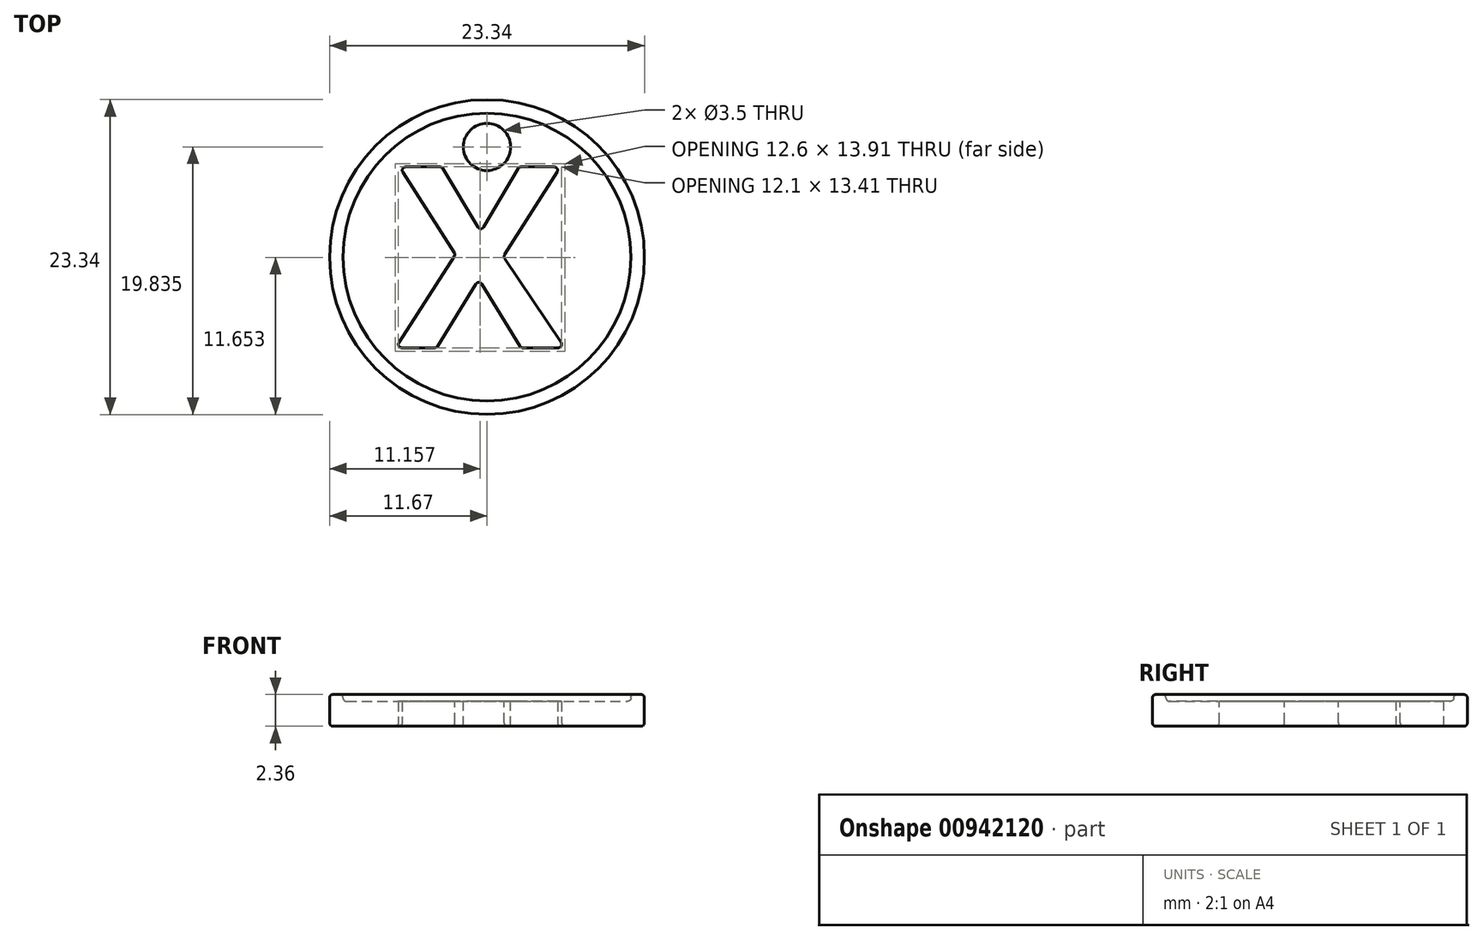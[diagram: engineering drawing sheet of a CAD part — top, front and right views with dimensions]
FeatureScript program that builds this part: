
annotation { "Feature Type Name" : "Feature", "Feature Type Description" : "" }
export const myFeature = defineFeature(function(context is Context, id is Id, definition is map)
    precondition{}
    {
        {
            var Q0;
            Q0=qCreatedBy(makeId("Front.planeOp"),FACE);
            var sketch = newSketch(context, id + "F0", { "sketchPlane" : qUnion([Q0])});
            skLineSegment(sketch, "E0", {"start": v(0, -1.17) * mm, "end": v(11.66, -1.17) * mm});
            skLineSegment(sketch, "E1", {"start": v(11.66, -1.17) * mm, "end": v(11.66, 1.17) * mm});
            skLineSegment(sketch, "E2", {"start": v(11.66, 1.17) * mm, "end": v(10.67, 1.17) * mm});
            skLineSegment(sketch, "E3", {"start": v(10.67, 1.17) * mm, "end": v(10.67, 0.67) * mm});
            skLineSegment(sketch, "E4", {"start": v(10.67, 0.67) * mm, "end": v(0, 0.67) * mm});
            skLineSegment(sketch, "E5", {"start": v(0, 0.67) * mm, "end": v(0, -1.17) * mm});
            skLineSegment(sketch, "E6", {"start": v(0, 5.9) * mm, "end": v(0, -4.97) * mm, "construction": true});
            skSolve(sketch);
        }
        {
            var Q0;
            Q0=makeQuery(id+"F0.imprint","IMPRINT",FACE,{"disambiguationData":[TD([[makeQuery(id+"F0.imprint","IMPRINT",EDGE,{"derivedFrom":sQuery(id+"F0.wireOp",EDGE,"E0")}),1.0]])]});
            var Q1;
            Q1=sQuery(id+"F0.wireOp",EDGE,"E6");
            revolve(context, id + "F1", {"surfaceOperationType" : NewSurfaceOperationType.NEW, "entities" : qUnion([Q0]), "axis" : qUnion([Q1]), "revolveType" : RevolveType.FULL});
        }
        {
            var Q0;
            Q0=makeQuery(id+"F1.opRevolve","SWEPT_FACE",FACE,{"disambiguationData":[OSD([sQuery(id+"F0.wireOp",EDGE,"E4")])]});
            var sketch = newSketch(context, id + "F2", { "sketchPlane" : qUnion([Q0])});
            skText(sketch, "E7", { "text": "X", "fontName": "OpenSans-Bold.ttf"});
            const initialGuessF2  = {"E7": [-0.00677, -0.00672, 1, 0, 0.01352]};
            skSetInitialGuess(sketch, initialGuessF2);
            skSolve(sketch);
        }
        {
            var Q0;
            Q0=makeQuery(id+"F2.imprint","IMPRINT",FACE,{"disambiguationData":[TD([[makeQuery(id+"F2.imprint","IMPRINT",EDGE,{"derivedFrom":sQuery(id+"F2.wireOp",EDGE,"E7.sketch_text.stroke-0")}),-1.0]])]});
            extrude(context, id + "F3", {"entities" : qUnion([Q0]), "operationType" : NewBodyOperationType.REMOVE, "oppositeDirection" : true, "depth" : 25 * mm, "offsetDistance" : 25 * mm});
        }
        {
            var Q0;
            Q0=makeQuery(id+"F1.opRevolve","SWEPT_EDGE",EDGE,{"disambiguationData":[OSD([sQuery(id+"F0.wireOp",EDGE,"E1"),sQuery(id+"F0.wireOp",EDGE,"E2")])]});
            var Q1;
            Q1=makeQuery(id+"F3.boolean.opBoolean","COPY",EDGE,{"derivedFrom":makeQuery(id+"F3.opExtrude","CAP_EDGE",EDGE,{"disambiguationData":[OSD([sQuery(id+"F2.wireOp",EDGE,"E7.sketch_text.stroke-5")])],"isStart":true})});
            var Q2;
            Q2=makeQuery(id+"F1.opRevolve","SWEPT_EDGE",EDGE,{"disambiguationData":[OSD([sQuery(id+"F0.wireOp",EDGE,"E0"),sQuery(id+"F0.wireOp",EDGE,"E1")])]});
            var Q3;
            Q3=makeQuery(id+"F1.opRevolve","SWEPT_EDGE",EDGE,{"disambiguationData":[OSD([sQuery(id+"F0.wireOp",EDGE,"E2"),sQuery(id+"F0.wireOp",EDGE,"E3")])]});
            var Q4;
            Q4=makeQuery(id+"F1.opRevolve","SWEPT_EDGE",EDGE,{"disambiguationData":[OSD([sQuery(id+"F0.wireOp",EDGE,"E3"),sQuery(id+"F0.wireOp",EDGE,"E4")])]});
            var Q5;
            Q5=makeQuery(id+"F3.boolean.opBoolean","COPY",EDGE,{"derivedFrom":makeQuery(id+"F3.opExtrude","CAP_EDGE",EDGE,{"disambiguationData":[OSD([sQuery(id+"F2.wireOp",EDGE,"E7.sketch_text.stroke-1")])],"isStart":true})});
            var Q6;
            Q6=makeQuery(id+"F3.boolean.opBoolean","INTERSECT",EDGE,{"derivedFrom":[makeQuery(id+"F1.opRevolve","SWEPT_FACE",FACE,{"disambiguationData":[OSD([sQuery(id+"F0.wireOp",EDGE,"E0")])]}),makeQuery(id+"F3.opExtrude","SWEPT_FACE",FACE,{"disambiguationData":[OSD([sQuery(id+"F2.wireOp",EDGE,"E7.sketch_text.stroke-7")])]})]});
            var Q7;
            Q7=makeQuery(id+"F3.boolean.opBoolean","COPY",EDGE,{"derivedFrom":makeQuery(id+"F3.opExtrude","CAP_EDGE",EDGE,{"disambiguationData":[OSD([sQuery(id+"F2.wireOp",EDGE,"E7.sketch_text.stroke-7")])],"isStart":true})});
            var Q8;
            Q8=makeQuery(id+"F3.boolean.opBoolean","INTERSECT",EDGE,{"derivedFrom":[makeQuery(id+"F1.opRevolve","SWEPT_FACE",FACE,{"disambiguationData":[OSD([sQuery(id+"F0.wireOp",EDGE,"E0")])]}),makeQuery(id+"F3.opExtrude","SWEPT_FACE",FACE,{"disambiguationData":[OSD([sQuery(id+"F2.wireOp",EDGE,"E7.sketch_text.stroke-11")])]})]});
            var Q9;
            Q9=makeQuery(id+"F3.boolean.opBoolean","COPY",EDGE,{"derivedFrom":makeQuery(id+"F3.opExtrude","CAP_EDGE",EDGE,{"disambiguationData":[OSD([sQuery(id+"F2.wireOp",EDGE,"E7.sketch_text.stroke-9")])],"isStart":true})});
            var Q10;
            Q10=makeQuery(id+"F3.boolean.opBoolean","COPY",EDGE,{"derivedFrom":makeQuery(id+"F3.opExtrude","CAP_EDGE",EDGE,{"disambiguationData":[OSD([sQuery(id+"F2.wireOp",EDGE,"E7.sketch_text.stroke-11")])],"isStart":true})});
            var Q11;
            Q11=makeQuery(id+"F3.boolean.opBoolean","COPY",EDGE,{"derivedFrom":makeQuery(id+"F3.opExtrude","CAP_EDGE",EDGE,{"disambiguationData":[OSD([sQuery(id+"F2.wireOp",EDGE,"E7.sketch_text.stroke-2")])],"isStart":true})});
            var Q12;
            Q12=makeQuery(id+"F3.boolean.opBoolean","COPY",EDGE,{"derivedFrom":makeQuery(id+"F3.opExtrude","CAP_EDGE",EDGE,{"disambiguationData":[OSD([sQuery(id+"F2.wireOp",EDGE,"E7.sketch_text.stroke-3")])],"isStart":true})});
            var Q13;
            Q13=makeQuery(id+"F3.boolean.opBoolean","COPY",EDGE,{"derivedFrom":makeQuery(id+"F3.opExtrude","SWEPT_EDGE",EDGE,{"disambiguationData":[OSD([sQuery(id+"F2.wireOp",EDGE,"E7.sketch_text.stroke-0"),sQuery(id+"F2.wireOp",EDGE,"E7.sketch_text.stroke-11")])]})});
            var Q14;
            Q14=makeQuery(id+"F3.boolean.opBoolean","COPY",EDGE,{"derivedFrom":makeQuery(id+"F3.opExtrude","SWEPT_EDGE",EDGE,{"disambiguationData":[OSD([sQuery(id+"F2.wireOp",EDGE,"E7.sketch_text.stroke-0"),sQuery(id+"F2.wireOp",EDGE,"E7.sketch_text.stroke-1")])]})});
            var Q15;
            Q15=makeQuery(id+"F3.boolean.opBoolean","COPY",EDGE,{"derivedFrom":makeQuery(id+"F3.opExtrude","SWEPT_EDGE",EDGE,{"disambiguationData":[OSD([sQuery(id+"F2.wireOp",EDGE,"E7.sketch_text.stroke-1"),sQuery(id+"F2.wireOp",EDGE,"E7.sketch_text.stroke-2")])]})});
            var Q16;
            Q16=makeQuery(id+"F3.boolean.opBoolean","COPY",EDGE,{"derivedFrom":makeQuery(id+"F3.opExtrude","SWEPT_EDGE",EDGE,{"disambiguationData":[OSD([sQuery(id+"F2.wireOp",EDGE,"E7.sketch_text.stroke-2"),sQuery(id+"F2.wireOp",EDGE,"E7.sketch_text.stroke-3")])]})});
            var Q17;
            Q17=makeQuery(id+"F3.boolean.opBoolean","COPY",EDGE,{"derivedFrom":makeQuery(id+"F3.opExtrude","SWEPT_EDGE",EDGE,{"disambiguationData":[OSD([sQuery(id+"F2.wireOp",EDGE,"E7.sketch_text.stroke-3"),sQuery(id+"F2.wireOp",EDGE,"E7.sketch_text.stroke-4")])]})});
            var Q18;
            Q18=makeQuery(id+"F3.boolean.opBoolean","COPY",EDGE,{"derivedFrom":makeQuery(id+"F3.opExtrude","SWEPT_EDGE",EDGE,{"disambiguationData":[OSD([sQuery(id+"F2.wireOp",EDGE,"E7.sketch_text.stroke-5"),sQuery(id+"F2.wireOp",EDGE,"E7.sketch_text.stroke-6")])]})});
            var Q19;
            Q19=makeQuery(id+"F3.boolean.opBoolean","COPY",EDGE,{"derivedFrom":makeQuery(id+"F3.opExtrude","SWEPT_EDGE",EDGE,{"disambiguationData":[OSD([sQuery(id+"F2.wireOp",EDGE,"E7.sketch_text.stroke-6"),sQuery(id+"F2.wireOp",EDGE,"E7.sketch_text.stroke-7")])]})});
            var Q20;
            Q20=makeQuery(id+"F3.boolean.opBoolean","COPY",EDGE,{"derivedFrom":makeQuery(id+"F3.opExtrude","SWEPT_EDGE",EDGE,{"disambiguationData":[OSD([sQuery(id+"F2.wireOp",EDGE,"E7.sketch_text.stroke-7"),sQuery(id+"F2.wireOp",EDGE,"E7.sketch_text.stroke-8")])]})});
            var Q21;
            Q21=makeQuery(id+"F3.boolean.opBoolean","COPY",EDGE,{"derivedFrom":makeQuery(id+"F3.opExtrude","SWEPT_EDGE",EDGE,{"disambiguationData":[OSD([sQuery(id+"F2.wireOp",EDGE,"E7.sketch_text.stroke-8"),sQuery(id+"F2.wireOp",EDGE,"E7.sketch_text.stroke-9")])]})});
            var Q22;
            Q22=makeQuery(id+"F3.boolean.opBoolean","COPY",EDGE,{"derivedFrom":makeQuery(id+"F3.opExtrude","SWEPT_EDGE",EDGE,{"disambiguationData":[OSD([sQuery(id+"F2.wireOp",EDGE,"E7.sketch_text.stroke-9"),sQuery(id+"F2.wireOp",EDGE,"E7.sketch_text.stroke-10")])]})});
            var Q23;
            Q23=makeQuery(id+"F3.boolean.opBoolean","COPY",EDGE,{"derivedFrom":makeQuery(id+"F3.opExtrude","SWEPT_EDGE",EDGE,{"disambiguationData":[OSD([sQuery(id+"F2.wireOp",EDGE,"E7.sketch_text.stroke-10"),sQuery(id+"F2.wireOp",EDGE,"E7.sketch_text.stroke-11")])]})});
            var Q24;
            Q24=makeQuery(id+"F3.boolean.opBoolean","COPY",EDGE,{"derivedFrom":makeQuery(id+"F3.opExtrude","CAP_EDGE",EDGE,{"disambiguationData":[OSD([sQuery(id+"F2.wireOp",EDGE,"E7.sketch_text.stroke-0")])],"isStart":true})});
            var Q25;
            Q25=makeQuery(id+"F3.boolean.opBoolean","INTERSECT",EDGE,{"derivedFrom":[makeQuery(id+"F1.opRevolve","SWEPT_FACE",FACE,{"disambiguationData":[OSD([sQuery(id+"F0.wireOp",EDGE,"E0")])]}),makeQuery(id+"F3.opExtrude","SWEPT_FACE",FACE,{"disambiguationData":[OSD([sQuery(id+"F2.wireOp",EDGE,"E7.sketch_text.stroke-5")])]})]});
            var Q26;
            Q26=makeQuery(id+"F3.boolean.opBoolean","INTERSECT",EDGE,{"derivedFrom":[makeQuery(id+"F1.opRevolve","SWEPT_FACE",FACE,{"disambiguationData":[OSD([sQuery(id+"F0.wireOp",EDGE,"E0")])]}),makeQuery(id+"F3.opExtrude","SWEPT_FACE",FACE,{"disambiguationData":[OSD([sQuery(id+"F2.wireOp",EDGE,"E7.sketch_text.stroke-6")])]})]});
            var Q27;
            Q27=makeQuery(id+"F3.boolean.opBoolean","COPY",EDGE,{"derivedFrom":makeQuery(id+"F3.opExtrude","CAP_EDGE",EDGE,{"disambiguationData":[OSD([sQuery(id+"F2.wireOp",EDGE,"E7.sketch_text.stroke-4")])],"isStart":true})});
            var Q28;
            Q28=makeQuery(id+"F3.boolean.opBoolean","INTERSECT",EDGE,{"derivedFrom":[makeQuery(id+"F1.opRevolve","SWEPT_FACE",FACE,{"disambiguationData":[OSD([sQuery(id+"F0.wireOp",EDGE,"E0")])]}),makeQuery(id+"F3.opExtrude","SWEPT_FACE",FACE,{"disambiguationData":[OSD([sQuery(id+"F2.wireOp",EDGE,"E7.sketch_text.stroke-8")])]})]});
            var Q29;
            Q29=makeQuery(id+"F3.boolean.opBoolean","INTERSECT",EDGE,{"derivedFrom":[makeQuery(id+"F1.opRevolve","SWEPT_FACE",FACE,{"disambiguationData":[OSD([sQuery(id+"F0.wireOp",EDGE,"E0")])]}),makeQuery(id+"F3.opExtrude","SWEPT_FACE",FACE,{"disambiguationData":[OSD([sQuery(id+"F2.wireOp",EDGE,"E7.sketch_text.stroke-9")])]})]});
            var Q30;
            Q30=makeQuery(id+"F3.boolean.opBoolean","COPY",EDGE,{"derivedFrom":makeQuery(id+"F3.opExtrude","CAP_EDGE",EDGE,{"disambiguationData":[OSD([sQuery(id+"F2.wireOp",EDGE,"E7.sketch_text.stroke-6")])],"isStart":true})});
            var Q31;
            Q31=makeQuery(id+"F3.boolean.opBoolean","INTERSECT",EDGE,{"derivedFrom":[makeQuery(id+"F1.opRevolve","SWEPT_FACE",FACE,{"disambiguationData":[OSD([sQuery(id+"F0.wireOp",EDGE,"E0")])]}),makeQuery(id+"F3.opExtrude","SWEPT_FACE",FACE,{"disambiguationData":[OSD([sQuery(id+"F2.wireOp",EDGE,"E7.sketch_text.stroke-10")])]})]});
            var Q32;
            Q32=makeQuery(id+"F3.boolean.opBoolean","COPY",EDGE,{"derivedFrom":makeQuery(id+"F3.opExtrude","CAP_EDGE",EDGE,{"disambiguationData":[OSD([sQuery(id+"F2.wireOp",EDGE,"E7.sketch_text.stroke-8")])],"isStart":true})});
            var Q33;
            Q33=makeQuery(id+"F3.boolean.opBoolean","COPY",EDGE,{"derivedFrom":makeQuery(id+"F3.opExtrude","CAP_EDGE",EDGE,{"disambiguationData":[OSD([sQuery(id+"F2.wireOp",EDGE,"E7.sketch_text.stroke-10")])],"isStart":true})});
            var Q34;
            Q34=makeQuery(id+"F3.boolean.opBoolean","INTERSECT",EDGE,{"derivedFrom":[makeQuery(id+"F1.opRevolve","SWEPT_FACE",FACE,{"disambiguationData":[OSD([sQuery(id+"F0.wireOp",EDGE,"E0")])]}),makeQuery(id+"F3.opExtrude","SWEPT_FACE",FACE,{"disambiguationData":[OSD([sQuery(id+"F2.wireOp",EDGE,"E7.sketch_text.stroke-0")])]})]});
            var Q35;
            Q35=makeQuery(id+"F3.boolean.opBoolean","INTERSECT",EDGE,{"derivedFrom":[makeQuery(id+"F1.opRevolve","SWEPT_FACE",FACE,{"disambiguationData":[OSD([sQuery(id+"F0.wireOp",EDGE,"E0")])]}),makeQuery(id+"F3.opExtrude","SWEPT_FACE",FACE,{"disambiguationData":[OSD([sQuery(id+"F2.wireOp",EDGE,"E7.sketch_text.stroke-1")])]})]});
            var Q36;
            Q36=makeQuery(id+"F3.boolean.opBoolean","INTERSECT",EDGE,{"derivedFrom":[makeQuery(id+"F1.opRevolve","SWEPT_FACE",FACE,{"disambiguationData":[OSD([sQuery(id+"F0.wireOp",EDGE,"E0")])]}),makeQuery(id+"F3.opExtrude","SWEPT_FACE",FACE,{"disambiguationData":[OSD([sQuery(id+"F2.wireOp",EDGE,"E7.sketch_text.stroke-2")])]})]});
            var Q37;
            Q37=makeQuery(id+"F3.boolean.opBoolean","INTERSECT",EDGE,{"derivedFrom":[makeQuery(id+"F1.opRevolve","SWEPT_FACE",FACE,{"disambiguationData":[OSD([sQuery(id+"F0.wireOp",EDGE,"E0")])]}),makeQuery(id+"F3.opExtrude","SWEPT_FACE",FACE,{"disambiguationData":[OSD([sQuery(id+"F2.wireOp",EDGE,"E7.sketch_text.stroke-3")])]})]});
            var Q38;
            Q38=makeQuery(id+"F3.boolean.opBoolean","INTERSECT",EDGE,{"derivedFrom":[makeQuery(id+"F1.opRevolve","SWEPT_FACE",FACE,{"disambiguationData":[OSD([sQuery(id+"F0.wireOp",EDGE,"E0")])]}),makeQuery(id+"F3.opExtrude","SWEPT_FACE",FACE,{"disambiguationData":[OSD([sQuery(id+"F2.wireOp",EDGE,"E7.sketch_text.stroke-4")])]})]});
            var Q39;
            Q39=makeQuery(id+"F3.boolean.opBoolean","COPY",EDGE,{"derivedFrom":makeQuery(id+"F3.opExtrude","SWEPT_EDGE",EDGE,{"disambiguationData":[OSD([sQuery(id+"F2.wireOp",EDGE,"E7.sketch_text.stroke-4"),sQuery(id+"F2.wireOp",EDGE,"E7.sketch_text.stroke-5")])]})});
            fillet(context, id + "F4", {"entities" : qUnion([Q0, Q1, Q2, Q3, Q4, Q5, Q6, Q7, Q8, Q9, Q10, Q11, Q12, Q13, Q14, Q15, Q16, Q17, Q18, Q19, Q20, Q21, Q22, Q23, Q24, Q25, Q26, Q27, Q28, Q29, Q30, Q31, Q32, Q33, Q34, Q35, Q36, Q37, Q38, Q39]), "radius" : 0.25 * mm, "tangentPropagation" : true, "allowEdgeOverflow" : false});
        }
        {
            var Q0;
            Q0=makeQuery(id+"F1.opRevolve","SWEPT_FACE",FACE,{"disambiguationData":[OSD([sQuery(id+"F0.wireOp",EDGE,"E4")])]});
            var sketch = newSketch(context, id + "F5", { "sketchPlane" : qUnion([Q0])});
            skPoint(sketch, "E8", {"position": v(0, 8.17) * mm});
            skSolve(sketch);
        }
        {
            var Q0;
            Q0=sQuery(id+"F5.wireOp",VERTEX,"E8");
            var Q1;
            Q1=makeQuery(id+"F1.opRevolve","SWEPT_BODY",BODY,{"disambiguationData":[OSD([sQuery(id+"F0.wireOp",EDGE,"E0"),sQuery(id+"F0.wireOp",EDGE,"E1"),sQuery(id+"F0.wireOp",EDGE,"E2"),sQuery(id+"F0.wireOp",EDGE,"E3"),sQuery(id+"F0.wireOp",EDGE,"E4"),sQuery(id+"F0.wireOp",EDGE,"E5")])]});
            hole(context, id + "F6", {"style" : HoleStyle.SIMPLE, "endStyle" : HoleEndStyle.THROUGH, "holeDiameter" : 3.5 * mm, "majorDiameter" : 5 * mm, "isTappedThrough" : true, "tappedDepth" : 12 * mm, "tapClearance" : 3, "locations" : qUnion([Q0]), "scope" : qUnion([Q1])});
        }
    });
